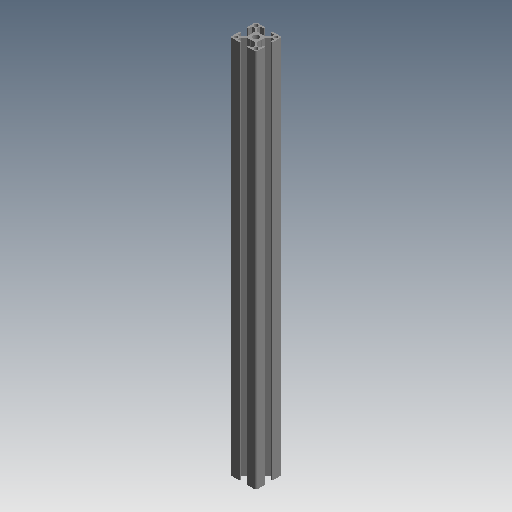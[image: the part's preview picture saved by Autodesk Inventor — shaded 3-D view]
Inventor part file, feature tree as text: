
AUTODESK INVENTOR PART (.ipt)
format: ipt  version: 2020 (Build 240168000, 168)  size: 211,456 bytes
history: native  units: mm (DEFAULTED — no unit token found)
features: other x21, sketch x3, hole x2, extrude x1, pattern_linear x1
ambient origin geometry x8: Origin, YZ Plane, XZ Plane, XY Plane, X Axis, Y Axis, Z Axis, Center Point
bodies: Solid1 (feature_tree)
feature tree (28):
  extrude  "Extrusion1"  Depth=440.0mm
  hole  "Hole1"  [1 undecoded]
  hole  "Hole2"  [1 undecoded]
  pattern_linear  "Rectangular Pattern1"  [2 undecoded]
  other  "C1_XY"
  other  "C1_YZ"
  other  "C1_ZX"
  other  "C1_X"
  other  "C1_Y"
  other  "C1_Z"
  other  "C1_Center"
  other  "to_frame_cap1_XY"
  other  "to_frame_cap1_YZ"
  other  "to_frame_cap1_ZX"
  other  "to_frame_cap1_X"
  other  "to_frame_cap1_Y"
  other  "to_frame_cap1_Z"
  other  "to_frame_cap1_Center"
  other  "to_frame_cap2_XY"
  other  "to_frame_cap2_YZ"
  other  "to_frame_cap2_ZX"
  other  "to_frame_cap2_X"
  other  "to_frame_cap2_Y"
  other  "to_frame_cap2_Z"
  other  "to_frame_cap2_Center"
  sketch  "Sketch_1"  dims[d0=440.0mm d1=0.0mm]
  sketch  "Sketch2"  dims[d2=6.8mm d3=6.0mm d4=4.0mm d5=2.0mm d6=90.0deg d7=440.0mm d8=0.0mm]
  sketch  "Sketch3"  dims[d9=4.2mm d10=6.0mm d11=4.0mm d12=2.0mm d13=90.0deg d14=440.0mm d15=0.0mm d16=20.0mm d18=23.2mm d19=20.0mm d21=23.2mm d22=0.0mm d23=0.0mm d24=0.0mm]
note: 4 required parameter values undecoded (feature->parameter linkage not recoverable at this tier; creation-order binding heuristic only, values carry confidence <= 0.55)
